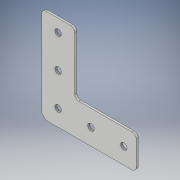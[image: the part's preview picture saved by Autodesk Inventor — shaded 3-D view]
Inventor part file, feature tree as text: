
AUTODESK INVENTOR PART (.ipt)
format: ipt  version: 2018 (Build 220112000, 112)  size: 162,304 bytes
history: native  units: in
note: dims shown in document units (in); Inventor stores cm internally (conversion verified against a paired STEP export)
features: extrude x3, sketch x3, fillet x1, chamfer x1
ambient origin geometry x8: Origin, YZ Plane, XZ Plane, XY Plane, X Axis, Y Axis, Z Axis, Center Point
bodies: Solid1 (feature_tree)
feature tree (8):
  extrude  "Extrusion1"  Depth=1.0in TaperAngle=0.0deg
  extrude  "Extrusion2"  Depth=0.125in
  extrude  "Extrusion3"  Depth=1.0in TaperAngle=0.0deg
  fillet  "Fillet2"  Radius=0.125in
  sketch  "Sketch1"  dims[d0=0.125in d1=1.0in d2=0.0in]
  sketch  "Sketch2"  dims[d4=0.0175in d5=0.0in d6=0.125in]
  sketch  "Sketch3"  dims[d7=0.125in d8=1.0in d9=0.0in d10=0.125in]
  chamfer  "Chamfer2"  [1 undecoded]
note: 1 required parameter value undecoded (feature->parameter linkage not recoverable at this tier; creation-order binding heuristic only, values carry confidence <= 0.55)
